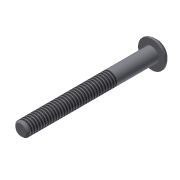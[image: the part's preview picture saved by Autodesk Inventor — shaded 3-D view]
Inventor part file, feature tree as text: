
AUTODESK INVENTOR PART (.ipt)
format: ipt  version: 2013 (Build 170138000, 138)  size: 123,904 bytes
history: native  units: in
note: dims shown in document units (in); Inventor stores cm internally (conversion verified against a paired STEP export)
features: sketch x3, extrude x2, revolve x1, chamfer x1, thread x1
ambient origin geometry x8: Origin, YZ Plane, XZ Plane, XY Plane, X Axis, Y Axis, Z Axis, Center Point
bodies: Solid1 (feature_tree)
feature tree (8):
  extrude  "Extrusion1"  Depth=1.5in TaperAngle=0.0deg
  revolve  "Revolution1"  [1 undecoded]
  extrude  "Extrusion2"  Depth=0.0938in
  chamfer  "Chamfer1"  Distance=0.0625in
  thread  "Thread1"  [1 undecoded]
  sketch  "Sketch1"  dims[d0=0.164in d1=1.5in d2=0.0in]
  sketch  "Sketch2"  dims[d3=0.087in d6=0.08in]
  sketch  "Sketch3"  dims[d7=90.0deg d8=0.0938in d9=0.0625in d10=0.0in d13=0.02in d14=0.125in d15=45.0deg d16=1.0in d17=0.0in d19=0.156in]
note: 2 required parameter values undecoded (feature->parameter linkage not recoverable at this tier; creation-order binding heuristic only, values carry confidence <= 0.55)